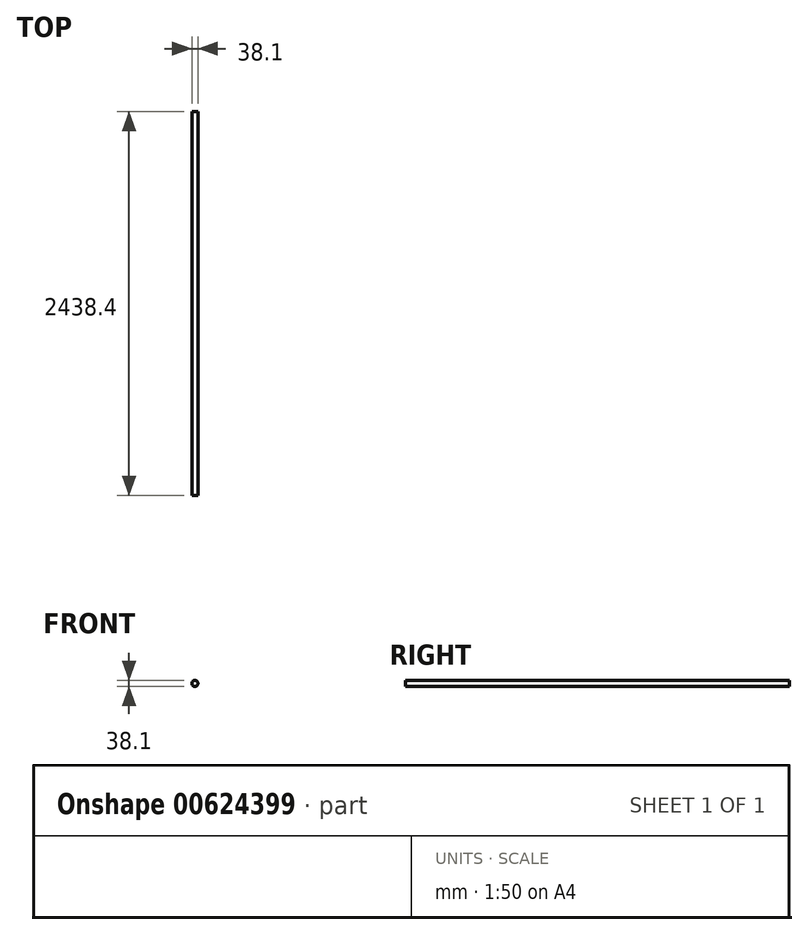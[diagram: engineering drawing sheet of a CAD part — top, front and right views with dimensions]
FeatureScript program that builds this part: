
annotation { "Feature Type Name" : "Feature", "Feature Type Description" : "" }
export const myFeature = defineFeature(function(context is Context, id is Id, definition is map)
    precondition{}
    {
        {
            var Q0;
            Q0=qCreatedBy(makeId("Front.planeOp"),FACE);
            var sketch = newSketch(context, id + "F0", { "sketchPlane" : qUnion([Q0])});
            skCircle(sketch, "E0", {"center": v(0, 0) * mm, "radius": 19.05 * mm});
            skSolve(sketch);
        }
        {
            var Q0;
            Q0 = qSketchRegion(id + "F0", true);
            extrude(context, id + "F1", {"entities" : qUnion([Q0]), "oppositeDirection" : true, "depth" : 2438.4 * mm, "offsetDistance" : 25 * mm});
        }
    });
